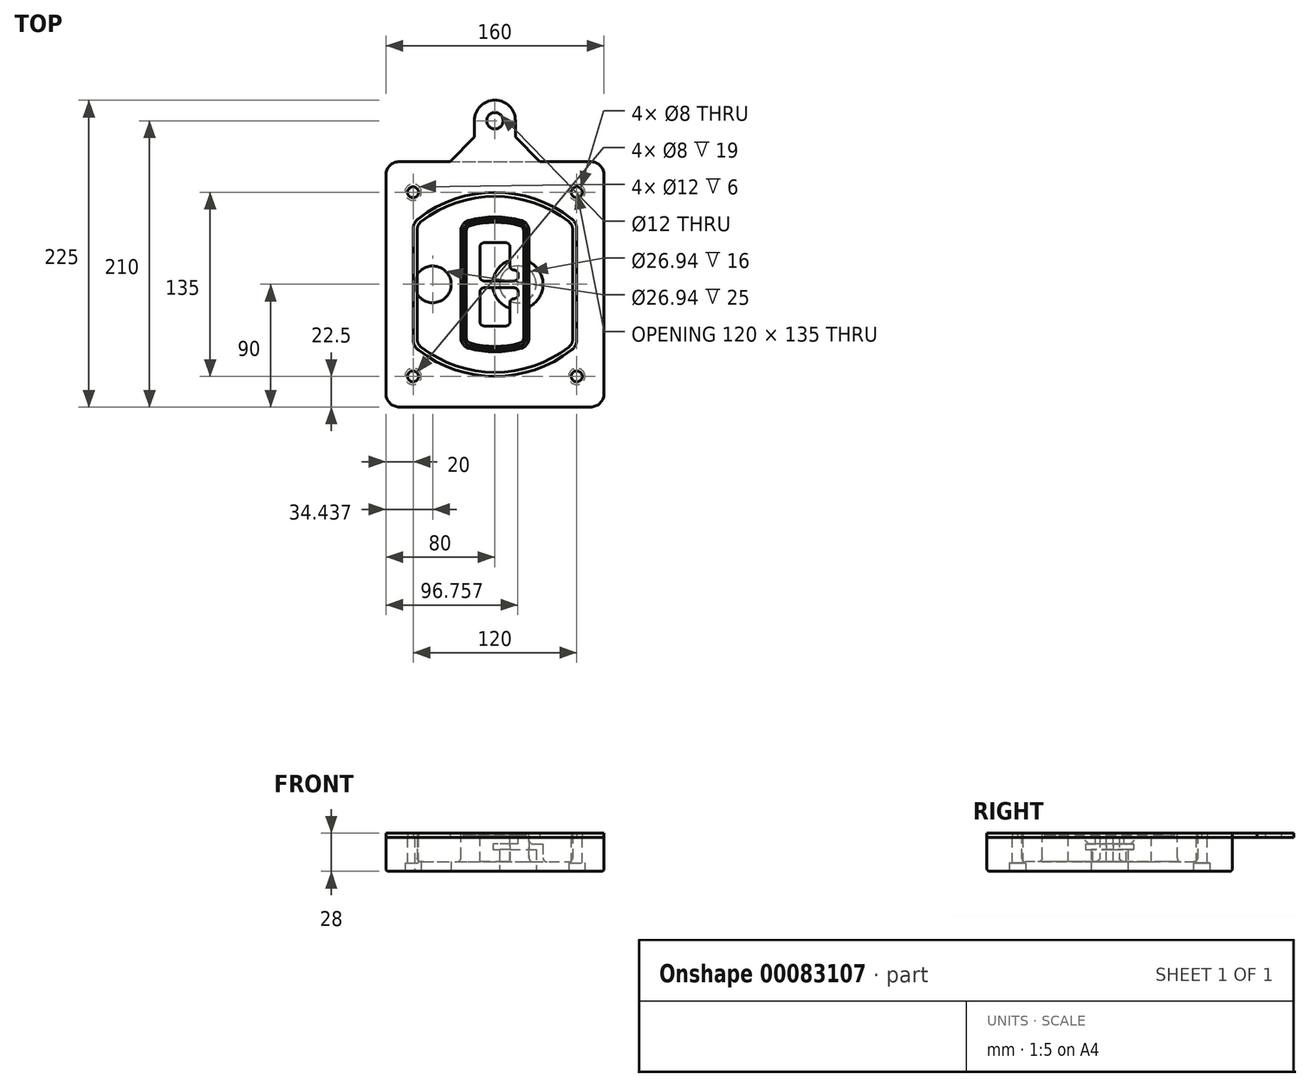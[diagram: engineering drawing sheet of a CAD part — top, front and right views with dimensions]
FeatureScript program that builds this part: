
annotation { "Feature Type Name" : "Feature", "Feature Type Description" : "" }
export const myFeature = defineFeature(function(context is Context, id is Id, definition is map)
    precondition{}
    {
        {
            var Q0;
            Q0=qCreatedBy(makeId("Top.planeOp"),FACE);
            var sketch = newSketch(context, id + "F0", { "sketchPlane" : qUnion([Q0])});
            skPoint(sketch, "E0.rect.middle", {"position": v(0, 0) * mm});
            skLineSegment(sketch, "E1.bottom", {"start": v(-70, -90) * mm, "end": v(70, -90) * mm});
            skLineSegment(sketch, "E1.top", {"start": v(-70, 90) * mm, "end": v(70, 90) * mm});
            skLineSegment(sketch, "E1.left", {"start": v(-80, -80) * mm, "end": v(-80, 80) * mm});
            skLineSegment(sketch, "E1.right", {"start": v(80, -80) * mm, "end": v(80, 80) * mm});
            skLineSegment(sketch, "E2", {"start": v(-80, 90) * mm, "end": v(80, -90) * mm, "construction": true});
            skLineSegment(sketch, "E3", {"start": v(80, 90) * mm, "end": v(-80, -90) * mm, "construction": true});
            skCircle(sketch, "E4", {"center": v(-60, 67.5) * mm, "radius": 4 * mm});
            skCircle(sketch, "E5", {"center": v(60, 67.5) * mm, "radius": 4 * mm});
            skCircle(sketch, "E6", {"center": v(60, -67.5) * mm, "radius": 4 * mm});
            skCircle(sketch, "E7", {"center": v(-60, -67.5) * mm, "radius": 4 * mm});
            skLineSegment(sketch, "E8", {"start": v(-60, 67.5) * mm, "end": v(60, 67.5) * mm, "construction": true});
            skLineSegment(sketch, "E9", {"start": v(60, 67.5) * mm, "end": v(60, -67.5) * mm, "construction": true});
            skLineSegment(sketch, "E10", {"start": v(60, -67.5) * mm, "end": v(-60, -67.5) * mm, "construction": true});
            skLineSegment(sketch, "E11", {"start": v(-60, -67.5) * mm, "end": v(-60, 67.5) * mm, "construction": true});
            skLineSegment(sketch, "E12", {"start": v(-60, 40.3) * mm, "end": v(-60, -40.3) * mm});
            skLineSegment(sketch, "E13", {"start": v(60, 40.3) * mm, "end": v(60, -40.3) * mm});
            skArc(sketch, "E14", {"start": v(56.15, 48.18) * mm, "mid": v(0, 67.5) * mm, "end": v(-56.15, 48.18) * mm});
            skArc(sketch, "E15", {"start": v(-56.15, -48.18) * mm, "mid": v(0, -67.5) * mm, "end": v(56.15, -48.18) * mm});
            skLineSegment(sketch, "E16", {"start": v(-60, 0) * mm, "end": v(60, 0) * mm, "construction": true});
            skPoint(sketch, "E17.visualSharp", {"position": v(-60, -45) * mm});
            skArc(sketch, "E17.filletArc", {"start": v(-60, -40.3) * mm, "mid": v(-58.99, -44.68) * mm, "end": v(-56.15, -48.18) * mm});
            skPoint(sketch, "E18.visualSharp", {"position": v(-60, 45) * mm});
            skArc(sketch, "E18.filletArc", {"start": v(-56.15, 48.18) * mm, "mid": v(-58.99, 44.68) * mm, "end": v(-60, 40.3) * mm});
            skPoint(sketch, "E19.visualSharp", {"position": v(60, 45) * mm});
            skArc(sketch, "E19.filletArc", {"start": v(60, 40.3) * mm, "mid": v(58.99, 44.68) * mm, "end": v(56.15, 48.18) * mm});
            skPoint(sketch, "E20.visualSharp", {"position": v(60, -45) * mm});
            skArc(sketch, "E20.filletArc", {"start": v(56.15, -48.18) * mm, "mid": v(58.99, -44.68) * mm, "end": v(60, -40.3) * mm});
            skPoint(sketch, "E21.visualSharp", {"position": v(-80, 90) * mm});
            skArc(sketch, "E21.filletArc", {"start": v(-70, 90) * mm, "mid": v(-77.07, 87.07) * mm, "end": v(-80, 80) * mm});
            skPoint(sketch, "E22.visualSharp", {"position": v(80, 90) * mm});
            skArc(sketch, "E22.filletArc", {"start": v(80, 80) * mm, "mid": v(77.07, 87.07) * mm, "end": v(70, 90) * mm});
            skPoint(sketch, "E23.visualSharp", {"position": v(80, -90) * mm});
            skArc(sketch, "E23.filletArc", {"start": v(70, -90) * mm, "mid": v(77.07, -87.07) * mm, "end": v(80, -80) * mm});
            skPoint(sketch, "E24.visualSharp", {"position": v(-80, -90) * mm});
            skArc(sketch, "E24.filletArc", {"start": v(-80, -80) * mm, "mid": v(-77.07, -87.07) * mm, "end": v(-70, -90) * mm});
            skArc(sketch, "E25.0", {"start": v(57, 40.3) * mm, "mid": v(56.3, 43.36) * mm, "end": v(54.3, 45.81) * mm});
            skLineSegment(sketch, "E25.1", {"start": v(57, 40.3) * mm, "end": v(57, -40.3) * mm});
            skArc(sketch, "E25.2", {"start": v(54.3, -45.81) * mm, "mid": v(56.3, -43.36) * mm, "end": v(57, -40.3) * mm});
            skArc(sketch, "E25.3", {"start": v(-54.3, -45.81) * mm, "mid": v(0, -64.5) * mm, "end": v(54.3, -45.81) * mm});
            skArc(sketch, "E25.4", {"start": v(-57, -40.3) * mm, "mid": v(-56.3, -43.36) * mm, "end": v(-54.3, -45.81) * mm});
            skArc(sketch, "E25.5", {"start": v(54.3, 45.81) * mm, "mid": v(0, 64.5) * mm, "end": v(-54.3, 45.81) * mm});
            skLineSegment(sketch, "E25.6", {"start": v(-57, 40.3) * mm, "end": v(-57, -40.3) * mm});
            skArc(sketch, "E25.7", {"start": v(-54.3, 45.81) * mm, "mid": v(-56.3, 43.36) * mm, "end": v(-57, 40.3) * mm});
            skArc(sketch, "E26.0", {"start": v(-58.62, 51.33) * mm, "mid": v(-62.58, 46.43) * mm, "end": v(-64, 40.3) * mm});
            skArc(sketch, "E26.1", {"start": v(58.62, 51.33) * mm, "mid": v(0, 71.5) * mm, "end": v(-58.62, 51.33) * mm});
            skArc(sketch, "E26.2", {"start": v(64, 40.3) * mm, "mid": v(62.58, 46.43) * mm, "end": v(58.62, 51.33) * mm});
            skLineSegment(sketch, "E26.3", {"start": v(64, 40.3) * mm, "end": v(64, -40.3) * mm});
            skArc(sketch, "E26.4", {"start": v(58.62, -51.33) * mm, "mid": v(62.58, -46.43) * mm, "end": v(64, -40.3) * mm});
            skLineSegment(sketch, "E26.5", {"start": v(-64, 40.3) * mm, "end": v(-64, -40.3) * mm});
            skArc(sketch, "E26.6", {"start": v(-58.62, -51.33) * mm, "mid": v(0, -71.5) * mm, "end": v(58.62, -51.33) * mm});
            skArc(sketch, "E26.7", {"start": v(-64, -40.3) * mm, "mid": v(-62.58, -46.43) * mm, "end": v(-58.62, -51.33) * mm});
            skSolve(sketch);
        }
        {
            var Q0;
            Q0=makeQuery(id+"F0.imprint","IMPRINT",FACE,{"disambiguationData":[TD([[makeQuery(id+"F0.imprint","IMPRINT",EDGE,{"derivedFrom":sQuery(id+"F0.wireOp",EDGE,"E1.bottom")}),1.0]])]});
            var Q1;
            Q1=makeQuery(id+"F0.imprint","IMPRINT",FACE,{"disambiguationData":[TD([[makeQuery(id+"F0.imprint","IMPRINT",EDGE,{"derivedFrom":sQuery(id+"F0.wireOp",EDGE,"E12")}),1.0]])]});
            var Q2;
            Q2=makeQuery(id+"F0.imprint","IMPRINT",FACE,{"disambiguationData":[TD([[makeQuery(id+"F0.imprint","IMPRINT",EDGE,{"derivedFrom":sQuery(id+"F0.wireOp",EDGE,"E25.0")}),1.0]])]});
            var Q3;
            Q3=makeQuery(id+"F0.imprint","IMPRINT",FACE,{"disambiguationData":[TD([[makeQuery(id+"F0.imprint","IMPRINT",EDGE,{"derivedFrom":sQuery(id+"F0.wireOp",EDGE,"E12")}),-1.0]])]});
            extrude(context, id + "F1", {"entities" : qUnion([Q0, Q1, Q2, Q3]), "oppositeDirection" : true, "depth" : 25 * mm});
        }
        {
            var Q0;
            Q0=makeQuery(id+"F0.imprint","IMPRINT",FACE,{"disambiguationData":[TD([[makeQuery(id+"F0.imprint","IMPRINT",EDGE,{"derivedFrom":sQuery(id+"F0.wireOp",EDGE,"E12")}),1.0]])]});
            extrude(context, id + "F2", {"entities" : qUnion([Q0]), "operationType" : NewBodyOperationType.ADD, "depth" : 3 * mm});
        }
        {
            var Q0;
            Q0=makeQuery(id+"F0.imprint","IMPRINT",FACE,{"disambiguationData":[TD([[makeQuery(id+"F0.imprint","IMPRINT",EDGE,{"derivedFrom":sQuery(id+"F0.wireOp",EDGE,"E25.0")}),1.0]])]});
            extrude(context, id + "F3", {"entities" : qUnion([Q0]), "operationType" : NewBodyOperationType.REMOVE, "oppositeDirection" : true, "depth" : 18 * mm});
        }
        {
            var Q0;
            Q0=makeQuery(id+"F2.opExtrude","CAP_FACE",FACE,{"disambiguationData":[OSD([sQuery(id+"F0.wireOp",EDGE,"E12"),sQuery(id+"F0.wireOp",EDGE,"E13"),sQuery(id+"F0.wireOp",EDGE,"E14"),sQuery(id+"F0.wireOp",EDGE,"E15"),sQuery(id+"F0.wireOp",EDGE,"E17.filletArc"),sQuery(id+"F0.wireOp",EDGE,"E18.filletArc"),sQuery(id+"F0.wireOp",EDGE,"E19.filletArc"),sQuery(id+"F0.wireOp",EDGE,"E20.filletArc"),sQuery(id+"F0.wireOp",EDGE,"E25.0"),sQuery(id+"F0.wireOp",EDGE,"E25.1"),sQuery(id+"F0.wireOp",EDGE,"E25.2"),sQuery(id+"F0.wireOp",EDGE,"E25.3"),sQuery(id+"F0.wireOp",EDGE,"E25.4"),sQuery(id+"F0.wireOp",EDGE,"E25.5"),sQuery(id+"F0.wireOp",EDGE,"E25.6"),sQuery(id+"F0.wireOp",EDGE,"E25.7")])],"isStart":false});
            var sketch = newSketch(context, id + "F4", { "sketchPlane" : qUnion([Q0])});
            skArc(sketch, "E27.0", {"start": v(-19.08, -46.97) * mm, "mid": v(0, -49.5) * mm, "end": v(19.08, -46.97) * mm});
            skArc(sketch, "E28.0", {"start": v(19.08, 46.97) * mm, "mid": v(0, 49.5) * mm, "end": v(-19.08, 46.97) * mm});
            skLineSegment(sketch, "E29", {"start": v(-25, 39.25) * mm, "end": v(-25, -39.25) * mm});
            skLineSegment(sketch, "E30", {"start": v(25, 39.25) * mm, "end": v(25, -39.25) * mm});
            skLineSegment(sketch, "E31", {"start": v(-25, 45.1) * mm, "end": v(25, 45.1) * mm, "construction": true});
            skLineSegment(sketch, "E32", {"start": v(-25, -45.1) * mm, "end": v(25, -45.1) * mm, "construction": true});
            skPoint(sketch, "E33.visualSharp", {"position": v(-25, 45.1) * mm});
            skArc(sketch, "E33.filletArc", {"start": v(-19.08, 46.97) * mm, "mid": v(-23.35, 44.11) * mm, "end": v(-25, 39.25) * mm});
            skPoint(sketch, "E34.visualSharp", {"position": v(25, 45.1) * mm});
            skArc(sketch, "E34.filletArc", {"start": v(25, 39.25) * mm, "mid": v(23.35, 44.11) * mm, "end": v(19.08, 46.97) * mm});
            skPoint(sketch, "E35.visualSharp", {"position": v(25, -45.1) * mm});
            skArc(sketch, "E35.filletArc", {"start": v(19.08, -46.97) * mm, "mid": v(23.35, -44.11) * mm, "end": v(25, -39.25) * mm});
            skPoint(sketch, "E36.visualSharp", {"position": v(-25, -45.1) * mm});
            skArc(sketch, "E36.filletArc", {"start": v(-25, -39.25) * mm, "mid": v(-23.35, -44.11) * mm, "end": v(-19.08, -46.97) * mm});
            skArc(sketch, "E37.0", {"start": v(54.3, 45.81) * mm, "mid": v(0, 64.5) * mm, "end": v(-54.3, 45.81) * mm});
            skArc(sketch, "E37.1", {"start": v(-54.3, 45.81) * mm, "mid": v(-56.3, 43.36) * mm, "end": v(-57, 40.3) * mm});
            skLineSegment(sketch, "E37.2", {"start": v(-57, 40.3) * mm, "end": v(-57, -40.3) * mm});
            skArc(sketch, "E37.3", {"start": v(-57, -40.3) * mm, "mid": v(-56.3, -43.36) * mm, "end": v(-54.3, -45.81) * mm});
            skArc(sketch, "E37.4", {"start": v(-54.3, -45.81) * mm, "mid": v(0, -64.5) * mm, "end": v(54.3, -45.81) * mm});
            skArc(sketch, "E37.5", {"start": v(54.3, -45.81) * mm, "mid": v(56.3, -43.36) * mm, "end": v(57, -40.3) * mm});
            skLineSegment(sketch, "E37.6", {"start": v(57, 40.3) * mm, "end": v(57, -40.3) * mm});
            skArc(sketch, "E37.7", {"start": v(57, 40.3) * mm, "mid": v(56.3, 43.36) * mm, "end": v(54.3, 45.81) * mm});
            skLineSegment(sketch, "E38.0", {"start": v(23, 39.25) * mm, "end": v(23, -39.25) * mm});
            skArc(sketch, "E38.1", {"start": v(18.56, -45.04) * mm, "mid": v(21.76, -42.9) * mm, "end": v(23, -39.25) * mm});
            skArc(sketch, "E38.2", {"start": v(-18.56, -45.04) * mm, "mid": v(0, -47.5) * mm, "end": v(18.56, -45.04) * mm});
            skArc(sketch, "E38.3", {"start": v(-23, -39.25) * mm, "mid": v(-21.76, -42.9) * mm, "end": v(-18.56, -45.04) * mm});
            skLineSegment(sketch, "E38.4", {"start": v(-23, 39.25) * mm, "end": v(-23, -39.25) * mm});
            skArc(sketch, "E38.5", {"start": v(23, 39.25) * mm, "mid": v(21.76, 42.9) * mm, "end": v(18.56, 45.04) * mm});
            skArc(sketch, "E38.6", {"start": v(-18.56, 45.04) * mm, "mid": v(-21.76, 42.9) * mm, "end": v(-23, 39.25) * mm});
            skArc(sketch, "E38.7", {"start": v(18.56, 45.04) * mm, "mid": v(0, 47.5) * mm, "end": v(-18.56, 45.04) * mm});
            skArc(sketch, "E39.0", {"start": v(21, 39.25) * mm, "mid": v(20.18, 41.68) * mm, "end": v(18.04, 43.1) * mm});
            skLineSegment(sketch, "E39.1", {"start": v(21, 39.25) * mm, "end": v(21, -39.25) * mm});
            skArc(sketch, "E39.2", {"start": v(18.04, -43.1) * mm, "mid": v(20.18, -41.68) * mm, "end": v(21, -39.25) * mm});
            skArc(sketch, "E39.3", {"start": v(-18.04, -43.1) * mm, "mid": v(0, -45.5) * mm, "end": v(18.04, -43.1) * mm});
            skArc(sketch, "E39.4", {"start": v(-21, -39.25) * mm, "mid": v(-20.18, -41.68) * mm, "end": v(-18.04, -43.1) * mm});
            skArc(sketch, "E39.5", {"start": v(18.04, 43.1) * mm, "mid": v(0, 45.5) * mm, "end": v(-18.04, 43.1) * mm});
            skLineSegment(sketch, "E39.6", {"start": v(-21, 39.25) * mm, "end": v(-21, -39.25) * mm});
            skArc(sketch, "E39.7", {"start": v(-18.04, 43.1) * mm, "mid": v(-20.18, 41.68) * mm, "end": v(-21, 39.25) * mm});
            skLineSegment(sketch, "E40", {"start": v(-25, 0) * mm, "end": v(25, 0) * mm, "construction": true});
            skLineSegment(sketch, "E41", {"start": v(-11, 5.5) * mm, "end": v(-11, 27.5) * mm});
            skLineSegment(sketch, "E42", {"start": v(-8, 30.5) * mm, "end": v(8, 30.5) * mm});
            skLineSegment(sketch, "E43", {"start": v(11, 27.5) * mm, "end": v(11, 13.5) * mm});
            skLineSegment(sketch, "E44", {"start": v(14, 10.5) * mm, "end": v(14, 10.5) * mm});
            skLineSegment(sketch, "E45", {"start": v(17, 7.5) * mm, "end": v(17, 5.5) * mm});
            skLineSegment(sketch, "E46", {"start": v(14, 2.5) * mm, "end": v(-8, 2.5) * mm});
            skPoint(sketch, "E47.visualSharp", {"position": v(-11, 30.5) * mm});
            skArc(sketch, "E47.filletArc", {"start": v(-8, 30.5) * mm, "mid": v(-10.12, 29.62) * mm, "end": v(-11, 27.5) * mm});
            skPoint(sketch, "E48.visualSharp", {"position": v(11, 30.5) * mm});
            skArc(sketch, "E48.filletArc", {"start": v(11, 27.5) * mm, "mid": v(10.12, 29.62) * mm, "end": v(8, 30.5) * mm});
            skPoint(sketch, "E49.visualSharp", {"position": v(11, 10.5) * mm});
            skArc(sketch, "E49.filletArc", {"start": v(11, 13.5) * mm, "mid": v(11.88, 11.38) * mm, "end": v(14, 10.5) * mm});
            skPoint(sketch, "E50.visualSharp", {"position": v(17, 10.5) * mm});
            skArc(sketch, "E50.filletArc", {"start": v(17, 7.5) * mm, "mid": v(16.12, 9.62) * mm, "end": v(14, 10.5) * mm});
            skPoint(sketch, "E51.visualSharp", {"position": v(17, 2.5) * mm});
            skArc(sketch, "E51.filletArc", {"start": v(14, 2.5) * mm, "mid": v(16.12, 3.38) * mm, "end": v(17, 5.5) * mm});
            skPoint(sketch, "E52.visualSharp", {"position": v(-11, 2.5) * mm});
            skArc(sketch, "E52.filletArc", {"start": v(-11, 5.5) * mm, "mid": v(-10.12, 3.38) * mm, "end": v(-8, 2.5) * mm});
            skLineSegment(sketch, "E53.0.MirrorCS", {"start": v(14, -2.5) * mm, "end": v(-8, -2.5) * mm});
            skArc(sketch, "E54.0.MirrorCS", {"start": v(-11, -5.5) * mm, "mid": v(-10.12, -3.38) * mm, "end": v(-8, -2.5) * mm});
            skLineSegment(sketch, "E55.0.MirrorCS", {"start": v(-11, -5.5) * mm, "end": v(-11, -27.5) * mm});
            skArc(sketch, "E56.0.MirrorCS", {"start": v(-8, -30.5) * mm, "mid": v(-10.12, -29.62) * mm, "end": v(-11, -27.5) * mm});
            skLineSegment(sketch, "E57.0.MirrorCS", {"start": v(-8, -30.5) * mm, "end": v(8, -30.5) * mm});
            skArc(sketch, "E58.0.MirrorCS", {"start": v(11, -27.5) * mm, "mid": v(10.12, -29.62) * mm, "end": v(8, -30.5) * mm});
            skLineSegment(sketch, "E59.0.MirrorCS", {"start": v(11, -27.5) * mm, "end": v(11, -13.5) * mm});
            skArc(sketch, "E60.0.MirrorCS", {"start": v(11, -13.5) * mm, "mid": v(11.88, -11.38) * mm, "end": v(14, -10.5) * mm});
            skArc(sketch, "E61.0.MirrorCS", {"start": v(17, -7.5) * mm, "mid": v(16.12, -9.62) * mm, "end": v(14, -10.5) * mm});
            skLineSegment(sketch, "E62.0.MirrorCS", {"start": v(17, -7.5) * mm, "end": v(17, -5.5) * mm});
            skArc(sketch, "E63.0.MirrorCS", {"start": v(14, -2.5) * mm, "mid": v(16.12, -3.38) * mm, "end": v(17, -5.5) * mm});
            skSolve(sketch);
        }
        {
            var Q0;
            Q0=makeQuery(id+"F4.imprint","IMPRINT",FACE,{"disambiguationData":[TD([[makeQuery(id+"F4.imprint","IMPRINT",EDGE,{"derivedFrom":sQuery(id+"F4.wireOp",EDGE,"E27.0")}),1.0]])]});
            var Q1;
            Q1=makeQuery(id+"F4.imprint","IMPRINT",FACE,{"disambiguationData":[TD([[makeQuery(id+"F4.imprint","IMPRINT",EDGE,{"derivedFrom":sQuery(id+"F4.wireOp",EDGE,"E38.0")}),-1.0]])]});
            var Q2;
            Q2=makeQuery(id+"F4.imprint","IMPRINT",FACE,{"disambiguationData":[TD([[makeQuery(id+"F4.imprint","IMPRINT",EDGE,{"derivedFrom":sQuery(id+"F4.wireOp",EDGE,"E39.0")}),1.0]])]});
            extrude(context, id + "F5", {"entities" : qUnion([Q0, Q1, Q2]), "operationType" : NewBodyOperationType.ADD, "endBound" : BoundingType.UP_TO_NEXT, "oppositeDirection" : true, "depth" : 25 * mm});
        }
        {
            var Q0;
            Q0=makeQuery(id+"F4.imprint","IMPRINT",FACE,{"disambiguationData":[TD([[makeQuery(id+"F4.imprint","IMPRINT",EDGE,{"derivedFrom":sQuery(id+"F4.wireOp",EDGE,"E38.0")}),-1.0]])]});
            extrude(context, id + "F6", {"entities" : qUnion([Q0]), "operationType" : NewBodyOperationType.REMOVE, "oppositeDirection" : true, "depth" : 2 * mm});
        }
        {
            var Q0;
            Q0=makeQuery(id+"F1.opExtrude","CAP_FACE",FACE,{"disambiguationData":[OSD([sQuery(id+"F0.wireOp",EDGE,"E1.bottom"),sQuery(id+"F0.wireOp",EDGE,"E1.top"),sQuery(id+"F0.wireOp",EDGE,"E1.left"),sQuery(id+"F0.wireOp",EDGE,"E1.right"),sQuery(id+"F0.wireOp",EDGE,"E4"),sQuery(id+"F0.wireOp",EDGE,"E5"),sQuery(id+"F0.wireOp",EDGE,"E6"),sQuery(id+"F0.wireOp",EDGE,"E7"),sQuery(id+"F0.wireOp",EDGE,"E21.filletArc"),sQuery(id+"F0.wireOp",EDGE,"E22.filletArc"),sQuery(id+"F0.wireOp",EDGE,"E23.filletArc"),sQuery(id+"F0.wireOp",EDGE,"E24.filletArc")])],"isStart":false});
            var sketch = newSketch(context, id + "F7", { "sketchPlane" : qUnion([Q0])});
            skCircle(sketch, "E64", {"center": v(16.76, 0) * mm, "radius": 13.47 * mm});
            skCircle(sketch, "E65", {"center": v(-45.56, 0) * mm, "radius": 13.47 * mm});
            skLineSegment(sketch, "E66", {"start": v(80, 0) * mm, "end": v(-80, 0) * mm});
            skCircle(sketch, "E67", {"center": v(16.76, 0) * mm, "radius": 18.47 * mm});
            skCircle(sketch, "E68", {"center": v(60, -67.5) * mm, "radius": 6 * mm});
            skCircle(sketch, "E69", {"center": v(-60, -67.5) * mm, "radius": 6 * mm});
            skCircle(sketch, "E70", {"center": v(-60, 67.5) * mm, "radius": 6 * mm});
            skCircle(sketch, "E71", {"center": v(60, 67.5) * mm, "radius": 6 * mm});
            skSolve(sketch);
        }
        {
            var Q0;
            {var subQ1=sQuery(id+"F7.wireOp",EDGE,"E66");var subQ4=sQuery(id+"F7.wireOp",EDGE,"E64");var subQ6=makeQuery(id+"F7.imprint","INTERSECT",VERTEX,{"disambiguationData":[OD(0.0)],"derivedFrom":[subQ4,subQ1]});Q0=makeQuery(id+"F7.imprint","IMPRINT",FACE,{"disambiguationData":[TD([[makeQuery(id+"F7.imprint","IMPRINT",EDGE,{"disambiguationData":[TD([[subQ6,-1.0]])],"derivedFrom":subQ4}),-1.0]])]});}
            var Q1;
            {var subQ0=sQuery(id+"F7.wireOp",EDGE,"E66");var subQ1=sQuery(id+"F7.wireOp",EDGE,"E64");var subQ3=makeQuery(id+"F7.imprint","INTERSECT",VERTEX,{"disambiguationData":[OD(0.0)],"derivedFrom":[subQ1,subQ0]});Q1=makeQuery(id+"F7.imprint","IMPRINT",FACE,{"disambiguationData":[TD([[makeQuery(id+"F7.imprint","IMPRINT",EDGE,{"disambiguationData":[TD([[subQ3,-1.0]])],"derivedFrom":subQ1}),1.0]])]});}
            var Q2;
            {var subQ0=sQuery(id+"F7.wireOp",EDGE,"E66");var subQ1=sQuery(id+"F7.wireOp",EDGE,"E64");var subQ3=makeQuery(id+"F7.imprint","INTERSECT",VERTEX,{"disambiguationData":[OD(0.0)],"derivedFrom":[subQ1,subQ0]});Q2=makeQuery(id+"F7.imprint","IMPRINT",FACE,{"disambiguationData":[TD([[makeQuery(id+"F7.imprint","IMPRINT",EDGE,{"disambiguationData":[TD([[subQ3,1.0]])],"derivedFrom":subQ1}),1.0]])]});}
            var Q3;
            {var subQ1=sQuery(id+"F7.wireOp",EDGE,"E66");var subQ4=sQuery(id+"F7.wireOp",EDGE,"E64");var subQ6=makeQuery(id+"F7.imprint","INTERSECT",VERTEX,{"disambiguationData":[OD(0.0)],"derivedFrom":[subQ4,subQ1]});Q3=makeQuery(id+"F7.imprint","IMPRINT",FACE,{"disambiguationData":[TD([[makeQuery(id+"F7.imprint","IMPRINT",EDGE,{"disambiguationData":[TD([[subQ6,1.0]])],"derivedFrom":subQ4}),-1.0]])]});}
            extrude(context, id + "F8", {"entities" : qUnion([Q0, Q1, Q2, Q3]), "operationType" : NewBodyOperationType.ADD, "oppositeDirection" : true, "depth" : 20 * mm});
        }
        {
            var Q0;
            {var subQ0=sQuery(id+"F7.wireOp",EDGE,"E66");var subQ1=sQuery(id+"F7.wireOp",EDGE,"E64");var subQ3=makeQuery(id+"F7.imprint","INTERSECT",VERTEX,{"disambiguationData":[OD(0.0)],"derivedFrom":[subQ1,subQ0]});Q0=makeQuery(id+"F7.imprint","IMPRINT",FACE,{"disambiguationData":[TD([[makeQuery(id+"F7.imprint","IMPRINT",EDGE,{"disambiguationData":[TD([[subQ3,-1.0]])],"derivedFrom":subQ1}),1.0]])]});}
            var Q1;
            {var subQ0=sQuery(id+"F7.wireOp",EDGE,"E66");var subQ1=sQuery(id+"F7.wireOp",EDGE,"E64");var subQ3=makeQuery(id+"F7.imprint","INTERSECT",VERTEX,{"disambiguationData":[OD(0.0)],"derivedFrom":[subQ1,subQ0]});Q1=makeQuery(id+"F7.imprint","IMPRINT",FACE,{"disambiguationData":[TD([[makeQuery(id+"F7.imprint","IMPRINT",EDGE,{"disambiguationData":[TD([[subQ3,1.0]])],"derivedFrom":subQ1}),1.0]])]});}
            extrude(context, id + "F9", {"entities" : qUnion([Q0, Q1]), "operationType" : NewBodyOperationType.REMOVE, "oppositeDirection" : true, "depth" : 16 * mm});
        }
        {
            var Q0;
            {var subQ0=sQuery(id+"F7.wireOp",EDGE,"E66");var subQ1=sQuery(id+"F7.wireOp",EDGE,"E65");var subQ3=makeQuery(id+"F7.imprint","INTERSECT",VERTEX,{"disambiguationData":[OD(0.0)],"derivedFrom":[subQ1,subQ0]});Q0=makeQuery(id+"F7.imprint","IMPRINT",FACE,{"disambiguationData":[TD([[makeQuery(id+"F7.imprint","IMPRINT",EDGE,{"disambiguationData":[TD([[subQ3,-1.0]])],"derivedFrom":subQ1}),1.0]])]});}
            var Q1;
            {var subQ0=sQuery(id+"F7.wireOp",EDGE,"E66");var subQ1=sQuery(id+"F7.wireOp",EDGE,"E65");var subQ3=makeQuery(id+"F7.imprint","INTERSECT",VERTEX,{"disambiguationData":[OD(0.0)],"derivedFrom":[subQ1,subQ0]});Q1=makeQuery(id+"F7.imprint","IMPRINT",FACE,{"disambiguationData":[TD([[makeQuery(id+"F7.imprint","IMPRINT",EDGE,{"disambiguationData":[TD([[subQ3,1.0]])],"derivedFrom":subQ1}),1.0]])]});}
            extrude(context, id + "F10", {"entities" : qUnion([Q0, Q1]), "operationType" : NewBodyOperationType.REMOVE, "oppositeDirection" : true, "depth" : 25 * mm});
        }
        {
            var Q0;
            Q0=makeQuery(id+"F7.imprint","IMPRINT",FACE,{"disambiguationData":[TD([[makeQuery(id+"F7.imprint","IMPRINT",EDGE,{"derivedFrom":sQuery(id+"F7.wireOp",EDGE,"E68")}),1.0]])]});
            var Q1;
            Q1=makeQuery(id+"F7.imprint","IMPRINT",FACE,{"disambiguationData":[TD([[makeQuery(id+"F7.imprint","IMPRINT",EDGE,{"derivedFrom":makeQuery(id+"F1.opExtrude","CAP_EDGE",EDGE,{"disambiguationData":[OSD([sQuery(id+"F0.wireOp",EDGE,"E5")])],"isStart":false})}),-1.0]])]});
            var Q2;
            Q2=makeQuery(id+"F7.imprint","IMPRINT",FACE,{"disambiguationData":[TD([[makeQuery(id+"F7.imprint","IMPRINT",EDGE,{"derivedFrom":sQuery(id+"F7.wireOp",EDGE,"E69")}),1.0]])]});
            var Q3;
            Q3=makeQuery(id+"F7.imprint","IMPRINT",FACE,{"disambiguationData":[TD([[makeQuery(id+"F7.imprint","IMPRINT",EDGE,{"derivedFrom":makeQuery(id+"F1.opExtrude","CAP_EDGE",EDGE,{"disambiguationData":[OSD([sQuery(id+"F0.wireOp",EDGE,"E4")])],"isStart":false})}),-1.0]])]});
            var Q4;
            Q4=makeQuery(id+"F7.imprint","IMPRINT",FACE,{"disambiguationData":[TD([[makeQuery(id+"F7.imprint","IMPRINT",EDGE,{"derivedFrom":sQuery(id+"F7.wireOp",EDGE,"E70")}),1.0]])]});
            var Q5;
            Q5=makeQuery(id+"F7.imprint","IMPRINT",FACE,{"disambiguationData":[TD([[makeQuery(id+"F7.imprint","IMPRINT",EDGE,{"derivedFrom":makeQuery(id+"F1.opExtrude","CAP_EDGE",EDGE,{"disambiguationData":[OSD([sQuery(id+"F0.wireOp",EDGE,"E7")])],"isStart":false})}),-1.0]])]});
            var Q6;
            Q6=makeQuery(id+"F7.imprint","IMPRINT",FACE,{"disambiguationData":[TD([[makeQuery(id+"F7.imprint","IMPRINT",EDGE,{"derivedFrom":sQuery(id+"F7.wireOp",EDGE,"E71")}),1.0]])]});
            var Q7;
            Q7=makeQuery(id+"F7.imprint","IMPRINT",FACE,{"disambiguationData":[TD([[makeQuery(id+"F7.imprint","IMPRINT",EDGE,{"derivedFrom":makeQuery(id+"F1.opExtrude","CAP_EDGE",EDGE,{"disambiguationData":[OSD([sQuery(id+"F0.wireOp",EDGE,"E6")])],"isStart":false})}),-1.0]])]});
            extrude(context, id + "F11", {"entities" : qUnion([Q0, Q1, Q2, Q3, Q4, Q5, Q6, Q7]), "operationType" : NewBodyOperationType.REMOVE, "oppositeDirection" : true, "depth" : 6 * mm});
        }
        {
            var Q0;
            Q0=makeQuery(id+"F9.boolean.opBoolean","COPY",FACE,{"derivedFrom":makeQuery(id+"F9.opExtrude","CAP_FACE",FACE,{"disambiguationData":[OSD([sQuery(id+"F7.wireOp",EDGE,"E64")])],"isStart":false})});
            var sketch = newSketch(context, id + "F12", { "sketchPlane" : qUnion([Q0])});
            skArc(sketch, "E72.0", {"start": v(11, 17.55) * mm, "mid": v(2.57, 11.82) * mm, "end": v(-1.54, 2.5) * mm});
            skArc(sketch, "E72.1", {"start": v(-1.54, -2.5) * mm, "mid": v(2.57, -11.82) * mm, "end": v(11, -17.55) * mm});
            skLineSegment(sketch, "E73", {"start": v(-1.54, -2.5) * mm, "end": v(14, -2.5) * mm});
            skLineSegment(sketch, "E74.0", {"start": v(14, 2.5) * mm, "end": v(-1.54, 2.5) * mm});
            skArc(sketch, "E74.1", {"start": v(14, 2.5) * mm, "mid": v(16.12, 3.38) * mm, "end": v(17, 5.5) * mm});
            skLineSegment(sketch, "E74.2", {"start": v(17, 7.5) * mm, "end": v(17, 5.5) * mm});
            skArc(sketch, "E74.3", {"start": v(17, 7.5) * mm, "mid": v(16.12, 9.62) * mm, "end": v(14, 10.5) * mm});
            skArc(sketch, "E74.4", {"start": v(11, 13.5) * mm, "mid": v(11.88, 11.38) * mm, "end": v(14, 10.5) * mm});
            skLineSegment(sketch, "E74.5", {"start": v(11, 17.55) * mm, "end": v(11, 13.5) * mm});
            skLineSegment(sketch, "E74.7", {"start": v(14, -2.5) * mm, "end": v(-1.54, -2.5) * mm});
            skArc(sketch, "E74.8", {"start": v(14, -2.5) * mm, "mid": v(16.12, -3.38) * mm, "end": v(17, -5.5) * mm});
            skLineSegment(sketch, "E74.9", {"start": v(17, -7.5) * mm, "end": v(17, -5.5) * mm});
            skArc(sketch, "E74.10", {"start": v(17, -7.5) * mm, "mid": v(16.12, -9.62) * mm, "end": v(14, -10.5) * mm});
            skArc(sketch, "E74.11", {"start": v(11, -13.5) * mm, "mid": v(11.88, -11.38) * mm, "end": v(14, -10.5) * mm});
            skLineSegment(sketch, "E74.12", {"start": v(11, -17.55) * mm, "end": v(11, -13.5) * mm});
            skPoint(sketch, "E75.orphan", {"position": v(11, -27.5) * mm});
            skPoint(sketch, "E76.orphan", {"position": v(-8, -2.5) * mm});
            skPoint(sketch, "E77.orphan", {"position": v(-8, 2.5) * mm});
            skPoint(sketch, "E78.orphan", {"position": v(11, 27.5) * mm});
            skSolve(sketch);
        }
        {
            var Q0;
            {var subQ7=sQuery(id+"F12.wireOp",EDGE,"E72.0");var subQ14=sQuery(id+"F12.wireOp",EDGE,"E72.1");var subQ16=sQuery(id+"F12.wireOp",EDGE,"E74.1");var subQ18=sQuery(id+"F12.wireOp",EDGE,"E74.8");Q0=qUnion([makeQuery(id+"F12.imprint","IMPRINT",FACE,{"disambiguationData":[TD([[makeQuery(id+"F12.imprint","IMPRINT",EDGE,{"derivedFrom":subQ7}),1.0]])]}),makeQuery(id+"F12.imprint","IMPRINT",FACE,{"disambiguationData":[TD([[makeQuery(id+"F12.imprint","IMPRINT",EDGE,{"derivedFrom":subQ14}),1.0]])]}),makeQuery(id+"F12.imprint","IMPRINT",FACE,{"disambiguationData":[TD([[makeQuery(id+"F12.imprint","IMPRINT",EDGE,{"derivedFrom":subQ16}),1.0]])]}),makeQuery(id+"F12.imprint","IMPRINT",FACE,{"disambiguationData":[TD([[makeQuery(id+"F12.imprint","IMPRINT",EDGE,{"derivedFrom":subQ18}),-1.0]])]})]);}
            var Q1;
            Q1=makeQuery(id+"F5.boolean.opBoolean","SPLIT",FACE,{"disambiguationData":[TD([makeQuery(id+"F5.opExtrude","SWEPT_FACE",FACE,{"disambiguationData":[OSD([sQuery(id+"F4.wireOp",EDGE,"E41")])]})])],"derivedFrom":makeQuery(id+"F3.boolean.opBoolean","COPY",FACE,{"derivedFrom":makeQuery(id+"F3.opExtrude","CAP_FACE",FACE,{"disambiguationData":[OSD([sQuery(id+"F0.wireOp",EDGE,"E25.0"),sQuery(id+"F0.wireOp",EDGE,"E25.1"),sQuery(id+"F0.wireOp",EDGE,"E25.2"),sQuery(id+"F0.wireOp",EDGE,"E25.3"),sQuery(id+"F0.wireOp",EDGE,"E25.4"),sQuery(id+"F0.wireOp",EDGE,"E25.5"),sQuery(id+"F0.wireOp",EDGE,"E25.6"),sQuery(id+"F0.wireOp",EDGE,"E25.7")])],"isStart":false})})});
            extrude(context, id + "F13", {"entities" : qUnion([Q0]), "operationType" : NewBodyOperationType.REMOVE, "endBound" : BoundingType.UP_TO_SURFACE, "endBoundEntityFace" : qUnion([Q1]), "depth" : 25 * mm});
        }
        {
            var Q0;
            Q0=makeQuery(id+"F3.boolean.opBoolean","COPY",EDGE,{"derivedFrom":makeQuery(id+"F3.opExtrude","CAP_EDGE",EDGE,{"disambiguationData":[OSD([sQuery(id+"F0.wireOp",EDGE,"E25.6")])],"isStart":false})});
            var Q1;
            Q1=makeQuery(id+"F8.boolean.opBoolean","INTERSECT",EDGE,{"derivedFrom":[makeQuery(id+"F5.opExtrude","SWEPT_FACE",FACE,{"disambiguationData":[OSD([sQuery(id+"F4.wireOp",EDGE,"E30")])]}),makeQuery(id+"F8.opExtrude","CAP_FACE",FACE,{"disambiguationData":[OSD([sQuery(id+"F7.wireOp",EDGE,"E67")])],"isStart":false})]});
            var Q2;
            Q2=makeQuery(id+"F8.boolean.opBoolean","INTERSECT",EDGE,{"disambiguationData":[OD(1.0)],"derivedFrom":[makeQuery(id+"F5.opExtrude","SWEPT_FACE",FACE,{"disambiguationData":[OSD([sQuery(id+"F4.wireOp",EDGE,"E30")])]}),makeQuery(id+"F8.opExtrude","SWEPT_FACE",FACE,{"disambiguationData":[OSD([sQuery(id+"F7.wireOp",EDGE,"E67")])]})]});
            var Q3;
            {var subQ0=sQuery(id+"F4.wireOp",EDGE,"E30");Q3=makeQuery(id+"F8.boolean.opBoolean","SPLIT",EDGE,{"disambiguationData":[TD([makeQuery(id+"F5.opExtrude","SWEPT_FACE",FACE,{"disambiguationData":[OSD([sQuery(id+"F4.wireOp",EDGE,"E35.filletArc")])]})])],"derivedFrom":makeQuery(id+"F5.opExtrude","CAP_EDGE",EDGE,{"disambiguationData":[OSD([subQ0])],"isStart":false})});}
            var Q4;
            {var subQ0=sQuery(id+"F0.wireOp",EDGE,"E25.7");var subQ1=sQuery(id+"F0.wireOp",EDGE,"E25.1");var subQ2=sQuery(id+"F0.wireOp",EDGE,"E25.6");var subQ3=sQuery(id+"F0.wireOp",EDGE,"E25.5");var subQ4=sQuery(id+"F0.wireOp",EDGE,"E25.4");var subQ5=sQuery(id+"F0.wireOp",EDGE,"E25.0");var subQ6=sQuery(id+"F0.wireOp",EDGE,"E25.2");var subQ7=sQuery(id+"F0.wireOp",EDGE,"E25.3");Q4=makeQuery(id+"F8.boolean.opBoolean","INTERSECT",EDGE,{"derivedFrom":[makeQuery(id+"F5.boolean.opBoolean","SPLIT",FACE,{"disambiguationData":[TD([makeQuery(id+"F2.opExtrude","SWEPT_FACE",FACE,{"disambiguationData":[OSD([subQ5])]})])],"derivedFrom":makeQuery(id+"F3.boolean.opBoolean","COPY",FACE,{"derivedFrom":makeQuery(id+"F3.opExtrude","CAP_FACE",FACE,{"disambiguationData":[OSD([subQ5,subQ1,subQ6,subQ7,subQ4,subQ3,subQ2,subQ0])],"isStart":false})})}),makeQuery(id+"F8.opExtrude","SWEPT_FACE",FACE,{"disambiguationData":[OSD([sQuery(id+"F7.wireOp",EDGE,"E67")])]})]});}
            var Q5;
            Q5=makeQuery(id+"F8.boolean.opBoolean","INTERSECT",EDGE,{"disambiguationData":[OD(0.0)],"derivedFrom":[makeQuery(id+"F5.opExtrude","SWEPT_FACE",FACE,{"disambiguationData":[OSD([sQuery(id+"F4.wireOp",EDGE,"E30")])]}),makeQuery(id+"F8.opExtrude","SWEPT_FACE",FACE,{"disambiguationData":[OSD([sQuery(id+"F7.wireOp",EDGE,"E67")])]})]});
            fillet(context, id + "F14", {"entities" : qUnion([Q0, Q1, Q2, Q3, Q4, Q5]), "radius" : 3 * mm, "tangentPropagation" : true, "allowEdgeOverflow" : false});
        }
        {
            var Q0;
            Q0=makeQuery(id+"F1.opExtrude","CAP_EDGE",EDGE,{"disambiguationData":[OSD([sQuery(id+"F0.wireOp",EDGE,"E1.bottom")])],"isStart":false});
            fillet(context, id + "F15", {"entities" : qUnion([Q0]), "radius" : 2 * mm, "tangentPropagation" : true, "allowEdgeOverflow" : false});
        }
        {
            var Q0;
            {var subQ0=sQuery(id+"F0.wireOp",EDGE,"E22.filletArc");var subQ1=sQuery(id+"F0.wireOp",EDGE,"E7");var subQ2=sQuery(id+"F0.wireOp",EDGE,"E6");var subQ3=sQuery(id+"F0.wireOp",EDGE,"E5");var subQ4=sQuery(id+"F0.wireOp",EDGE,"E4");var subQ5=sQuery(id+"F0.wireOp",EDGE,"E1.bottom");var subQ6=sQuery(id+"F0.wireOp",EDGE,"E21.filletArc");var subQ7=sQuery(id+"F0.wireOp",EDGE,"E1.top");var subQ8=sQuery(id+"F0.wireOp",EDGE,"E1.left");var subQ9=sQuery(id+"F0.wireOp",EDGE,"E1.right");var subQ10=sQuery(id+"F0.wireOp",EDGE,"E23.filletArc");var subQ11=sQuery(id+"F0.wireOp",EDGE,"E24.filletArc");Q0=makeQuery(id+"F2.boolean.opBoolean","SPLIT",FACE,{"disambiguationData":[TD([makeQuery(id+"F1.opExtrude","SWEPT_FACE",FACE,{"disambiguationData":[OSD([subQ5])]})])],"derivedFrom":makeQuery(id+"F1.opExtrude","CAP_FACE",FACE,{"disambiguationData":[OSD([subQ5,subQ7,subQ8,subQ9,subQ4,subQ3,subQ2,subQ1,subQ6,subQ0,subQ10,subQ11])],"isStart":true})});}
            var sketch = newSketch(context, id + "F16", { "sketchPlane" : qUnion([Q0])});
            skCircle(sketch, "E79.1", {"center": v(-60, 67.5) * mm, "radius": 4 * mm});
            skCircle(sketch, "E79.2", {"center": v(60, 67.5) * mm, "radius": 4 * mm});
            skCircle(sketch, "E79.3", {"center": v(60, -67.5) * mm, "radius": 4 * mm});
            skCircle(sketch, "E79.4", {"center": v(-60, -67.5) * mm, "radius": 4 * mm});
            skPoint(sketch, "E79.5", {"position": v(-56.15, -48.18) * mm});
            skArc(sketch, "E79.6", {"start": v(-56.15, -48.18) * mm, "mid": v(0, -67.5) * mm, "end": v(56.15, -48.18) * mm});
            skArc(sketch, "E79.7", {"start": v(-60, -40.3) * mm, "mid": v(-58.99, -44.68) * mm, "end": v(-56.15, -48.18) * mm});
            skLineSegment(sketch, "E79.8", {"start": v(-60, 40.3) * mm, "end": v(-60, -40.3) * mm});
            skArc(sketch, "E79.9", {"start": v(-56.15, 48.18) * mm, "mid": v(-58.99, 44.68) * mm, "end": v(-60, 40.3) * mm});
            skArc(sketch, "E79.10", {"start": v(56.15, 48.18) * mm, "mid": v(0, 67.5) * mm, "end": v(-56.15, 48.18) * mm});
            skLineSegment(sketch, "E79.11", {"start": v(60, 40.3) * mm, "end": v(60, -40.3) * mm});
            skArc(sketch, "E79.12", {"start": v(56.15, -48.18) * mm, "mid": v(58.99, -44.68) * mm, "end": v(60, -40.3) * mm});
            skArc(sketch, "E79.13", {"start": v(60, 40.3) * mm, "mid": v(58.99, 44.68) * mm, "end": v(56.15, 48.18) * mm});
            skLineSegment(sketch, "E79.14", {"start": v(80, -80) * mm, "end": v(80, 80) * mm});
            skLineSegment(sketch, "E79.15", {"start": v(-70, -90) * mm, "end": v(70, -90) * mm});
            skArc(sketch, "E79.16", {"start": v(70, -90) * mm, "mid": v(77.07, -87.07) * mm, "end": v(80, -80) * mm});
            skArc(sketch, "E79.17", {"start": v(-80, -80) * mm, "mid": v(-77.07, -87.07) * mm, "end": v(-70, -90) * mm});
            skLineSegment(sketch, "E79.18", {"start": v(-80, -80) * mm, "end": v(-80, 80) * mm});
            skArc(sketch, "E79.19", {"start": v(-70, 90) * mm, "mid": v(-77.07, 87.07) * mm, "end": v(-80, 80) * mm});
            skLineSegment(sketch, "E79.20", {"start": v(-70, 90) * mm, "end": v(70, 90) * mm});
            skArc(sketch, "E79.21", {"start": v(80, 80) * mm, "mid": v(77.07, 87.07) * mm, "end": v(70, 90) * mm});
            skLineSegment(sketch, "E80", {"start": v(0, 90) * mm, "end": v(0, 120) * mm, "construction": true});
            skPoint(sketch, "E80.endSnap0", {"position": v(0, 90) * mm});
            skCircle(sketch, "E81", {"center": v(0, 120) * mm, "radius": 6 * mm});
            skLineSegment(sketch, "E82", {"start": v(-33, 90) * mm, "end": v(-15, 108) * mm});
            skLineSegment(sketch, "E83", {"start": v(-15, 108) * mm, "end": v(-15, 120) * mm});
            skLineSegment(sketch, "E84", {"start": v(33, 90) * mm, "end": v(15, 108) * mm});
            skLineSegment(sketch, "E85", {"start": v(15, 108) * mm, "end": v(15, 120) * mm});
            skArc(sketch, "E86", {"start": v(15, 120) * mm, "mid": v(0, 135) * mm, "end": v(-15, 120) * mm});
            skLineSegment(sketch, "E87", {"start": v(-80, 0) * mm, "end": v(80, 0) * mm, "construction": true});
            skArc(sketch, "E88.MirrorCS", {"start": v(15, -120) * mm, "mid": v(0, -135) * mm, "end": v(-15, -120) * mm});
            skCircle(sketch, "E89.MirrorC", {"center": v(0, -120) * mm, "radius": 6 * mm});
            skLineSegment(sketch, "E90.MirrorCS", {"start": v(15, -108) * mm, "end": v(15, -120) * mm});
            skLineSegment(sketch, "E91.MirrorCS", {"start": v(-15, -108) * mm, "end": v(-15, -120) * mm});
            skLineSegment(sketch, "E92.MirrorCS", {"start": v(33, -90) * mm, "end": v(15, -108) * mm});
            skLineSegment(sketch, "E93.MirrorCS", {"start": v(-33, -90) * mm, "end": v(-15, -108) * mm});
            skSolve(sketch);
        }
        {
            var Q0;
            Q0=makeQuery(id+"F16.imprint","IMPRINT",FACE,{"disambiguationData":[TD([[makeQuery(id+"F16.imprint","IMPRINT",EDGE,{"derivedFrom":sQuery(id+"F16.wireOp",EDGE,"E88.MirrorCS")}),-1.0]])]});
            var Q1;
            Q1=makeQuery(id+"F16.imprint","IMPRINT",FACE,{"disambiguationData":[TD([[makeQuery(id+"F16.imprint","IMPRINT",EDGE,{"derivedFrom":sQuery(id+"F16.wireOp",EDGE,"E81")}),-1.0]])]});
            var Q2;
            Q2=makeQuery(id+"F16.imprint","IMPRINT",FACE,{"disambiguationData":[TD([[makeQuery(id+"F16.imprint","IMPRINT",EDGE,{"derivedFrom":sQuery(id+"F16.wireOp",EDGE,"E79.1")}),-1.0]])]});
            var Q3;
            {var subQ0=sQuery(id+"F4.wireOp",EDGE,"E36.filletArc");var subQ1=sQuery(id+"F4.wireOp",EDGE,"E35.filletArc");var subQ2=sQuery(id+"F4.wireOp",EDGE,"E34.filletArc");var subQ3=sQuery(id+"F4.wireOp",EDGE,"E33.filletArc");var subQ4=sQuery(id+"F4.wireOp",EDGE,"E27.0");var subQ5=sQuery(id+"F4.wireOp",EDGE,"E30");var subQ6=sQuery(id+"F4.wireOp",EDGE,"E28.0");var subQ7=sQuery(id+"F4.wireOp",EDGE,"E29");Q3=makeQuery(id+"F6.boolean.opBoolean","SPLIT",FACE,{"disambiguationData":[TD([makeQuery(id+"F5.opExtrude","SWEPT_FACE",FACE,{"disambiguationData":[OSD([subQ4])]})])],"derivedFrom":makeQuery(id+"F5.opExtrude","CAP_FACE",FACE,{"disambiguationData":[OSD([subQ4,subQ6,subQ7,subQ5,subQ3,subQ2,subQ1,subQ0,sQuery(id+"F4.wireOp",EDGE,"E41"),sQuery(id+"F4.wireOp",EDGE,"E42"),sQuery(id+"F4.wireOp",EDGE,"E43"),sQuery(id+"F4.wireOp",EDGE,"E45"),sQuery(id+"F4.wireOp",EDGE,"E46"),sQuery(id+"F4.wireOp",EDGE,"E47.filletArc"),sQuery(id+"F4.wireOp",EDGE,"E48.filletArc"),sQuery(id+"F4.wireOp",EDGE,"E49.filletArc"),sQuery(id+"F4.wireOp",EDGE,"E50.filletArc"),sQuery(id+"F4.wireOp",EDGE,"E51.filletArc"),sQuery(id+"F4.wireOp",EDGE,"E52.filletArc"),sQuery(id+"F4.wireOp",EDGE,"E53.0.MirrorCS"),sQuery(id+"F4.wireOp",EDGE,"E54.0.MirrorCS"),sQuery(id+"F4.wireOp",EDGE,"E55.0.MirrorCS"),sQuery(id+"F4.wireOp",EDGE,"E56.0.MirrorCS"),sQuery(id+"F4.wireOp",EDGE,"E57.0.MirrorCS"),sQuery(id+"F4.wireOp",EDGE,"E58.0.MirrorCS"),sQuery(id+"F4.wireOp",EDGE,"E59.0.MirrorCS"),sQuery(id+"F4.wireOp",EDGE,"E60.0.MirrorCS"),sQuery(id+"F4.wireOp",EDGE,"E61.0.MirrorCS"),sQuery(id+"F4.wireOp",EDGE,"E62.0.MirrorCS"),sQuery(id+"F4.wireOp",EDGE,"E63.0.MirrorCS")])],"isStart":true})});}
            extrude(context, id + "F17", {"entities" : qUnion([Q0, Q1, Q2]), "endBound" : BoundingType.UP_TO_SURFACE, "endBoundEntityFace" : qUnion([Q3]), "depth" : 25 * mm});
        }
    });
